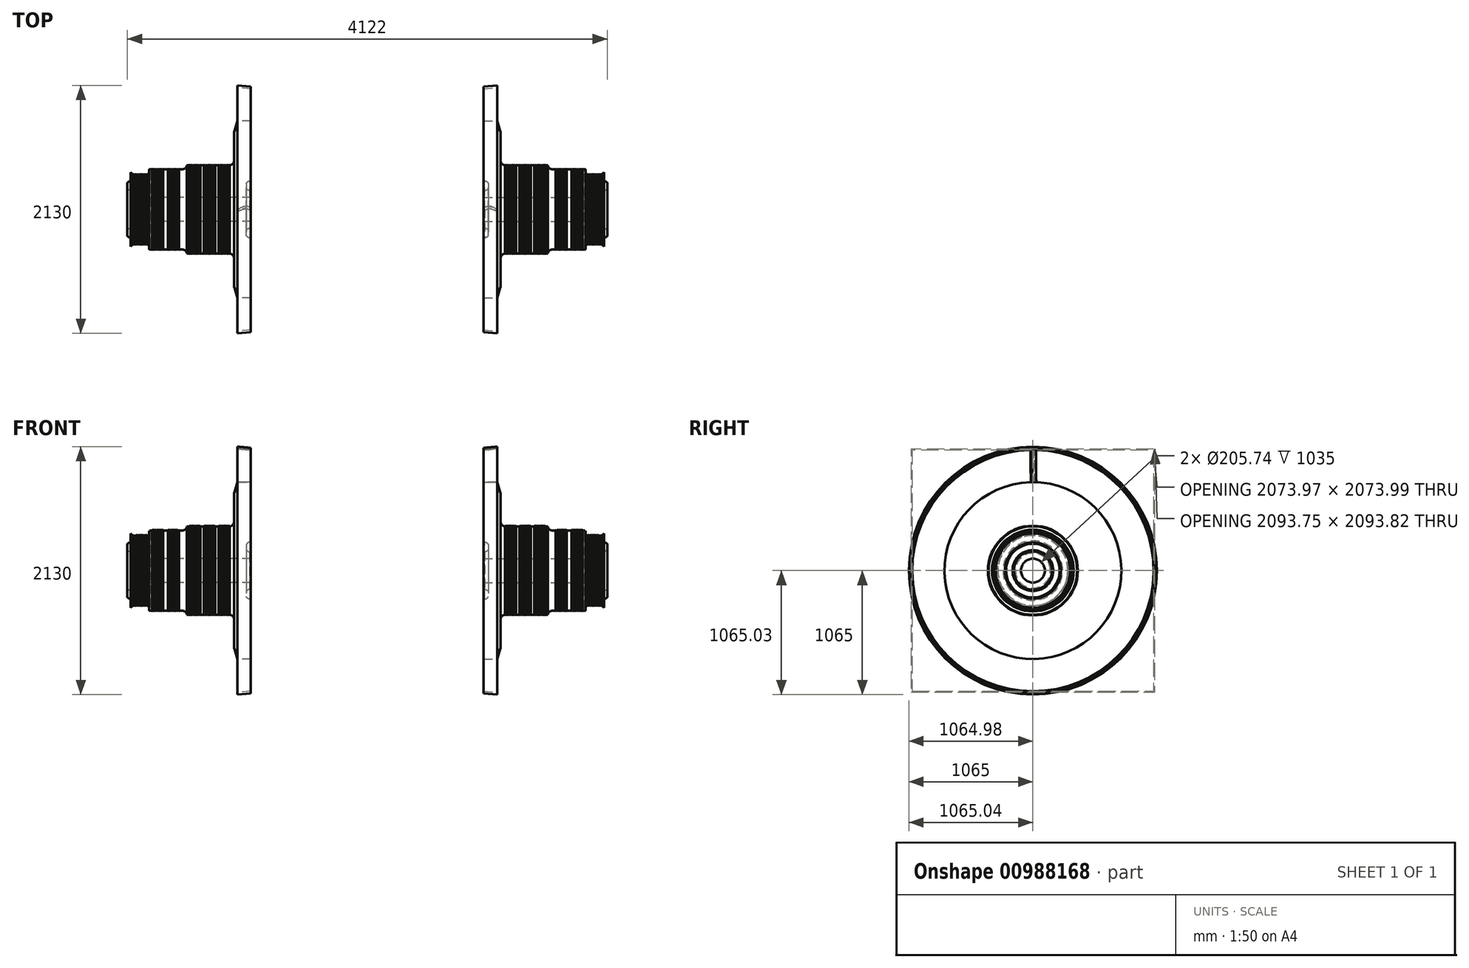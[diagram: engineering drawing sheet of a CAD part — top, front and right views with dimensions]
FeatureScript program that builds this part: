
annotation { "Feature Type Name" : "Feature", "Feature Type Description" : "" }
export const myFeature = defineFeature(function(context is Context, id is Id, definition is map)
    precondition{}
    {
        {
            var Q0;
            Q0=qCreatedBy(makeId("Top.planeOp"),FACE);
            var sketch = newSketch(context, id + "F0", { "sketchPlane" : qUnion([Q0])});
            skLineSegment(sketch, "E0", {"start": v(-458.73, 0) * mm, "end": v(0, 0) * mm, "construction": true});
            skLineSegment(sketch, "E1", {"start": v(0, 760) * mm, "end": v(-115, 760) * mm});
            skLineSegment(sketch, "E2", {"start": v(0, 102.87) * mm, "end": v(0, 157.87) * mm});
            skLineSegment(sketch, "E3", {"start": v(-115, 1065) * mm, "end": v(-115, 1047) * mm});
            skLineSegment(sketch, "E4", {"start": v(-115, 1047) * mm, "end": v(0, 1037) * mm});
            skLineSegment(sketch, "E5", {"start": v(0, 1037) * mm, "end": v(0, 1055) * mm});
            skLineSegment(sketch, "E6", {"start": v(0, 1055) * mm, "end": v(-115, 1065) * mm});
            skLineSegment(sketch, "E7", {"start": v(-115, 760) * mm, "end": v(-115, 1047) * mm, "construction": true});
            skLineSegment(sketch, "E8", {"start": v(-245, 202.87) * mm, "end": v(0, 202.87) * mm, "construction": true});
            skArc(sketch, "E9", {"start": v(0, 157.87) * mm, "mid": v(-22.53, 163.91) * mm, "end": v(-39, 180.42) * mm});
            skLineSegment(sketch, "E10", {"start": v(-39, 225.32) * mm, "end": v(-39, 180.42) * mm});
            skArc(sketch, "E11.trimOffspring", {"start": v(-39, 225.32) * mm, "mid": v(-22.53, 241.83) * mm, "end": v(0, 247.87) * mm});
            skLineSegment(sketch, "E12.trimOffspring", {"start": v(0, 247.87) * mm, "end": v(0, 760) * mm});
            skArc(sketch, "E13", {"start": v(0, 157.87) * mm, "mid": v(-45, 202.87) * mm, "end": v(0, 247.87) * mm, "construction": true});
            skLineSegment(sketch, "E14", {"start": v(0, 0) * mm, "end": v(1169.36, 0) * mm, "construction": true});
            skLineSegment(sketch, "E15", {"start": v(-115, 760) * mm, "end": v(-145, 665) * mm});
            skLineSegment(sketch, "E16", {"start": v(-145, 665) * mm, "end": v(-145, 380) * mm});
            skLineSegment(sketch, "E17", {"start": v(-145, 380) * mm, "end": v(-182, 380) * mm});
            skLineSegment(sketch, "E18", {"start": v(-550, 380) * mm, "end": v(-550, 345) * mm});
            skLineSegment(sketch, "E19", {"start": v(-550, 345) * mm, "end": v(-618, 345) * mm});
            skLineSegment(sketch, "E20", {"start": v(-870, 300) * mm, "end": v(-892, 300) * mm});
            skLineSegment(sketch, "E21", {"start": v(-1010, 300) * mm, "end": v(-1035, 320) * mm});
            skLineSegment(sketch, "E22", {"start": v(-1035, 320) * mm, "end": v(-1035, 240.87) * mm});
            skLineSegment(sketch, "E23", {"start": v(-1035, 102.87) * mm, "end": v(0, 102.87) * mm});
            skArc(sketch, "E24", {"start": v(-870, 345) * mm, "mid": v(-875, 340) * mm, "end": v(-870, 335) * mm});
            skLineSegment(sketch, "E25", {"start": v(-870, 335) * mm, "end": v(-870, 300) * mm});
            skLineSegment(sketch, "E26", {"start": v(-870, 345) * mm, "end": v(-870, 335) * mm, "construction": true});
            skLineSegment(sketch, "E27", {"start": v(-982, 306) * mm, "end": v(-898, 306) * mm, "construction": true});
            skLineSegment(sketch, "E28", {"start": v(-976, 300) * mm, "end": v(-970, 306) * mm});
            skLineSegment(sketch, "E29", {"start": v(-970, 306) * mm, "end": v(-964, 300) * mm});
            skLineSegment(sketch, "E30", {"start": v(-964, 300) * mm, "end": v(-958, 306) * mm});
            skLineSegment(sketch, "E31", {"start": v(-958, 306) * mm, "end": v(-952, 300) * mm});
            skLineSegment(sketch, "E32", {"start": v(-952, 300) * mm, "end": v(-946, 306) * mm});
            skLineSegment(sketch, "E33", {"start": v(-946, 306) * mm, "end": v(-940, 300) * mm});
            skLineSegment(sketch, "E34", {"start": v(-940, 300) * mm, "end": v(-934, 306) * mm});
            skLineSegment(sketch, "E35", {"start": v(-934, 306) * mm, "end": v(-928, 300) * mm});
            skLineSegment(sketch, "E36", {"start": v(-928, 300) * mm, "end": v(-922, 306) * mm});
            skLineSegment(sketch, "E37", {"start": v(-922, 306) * mm, "end": v(-916, 300) * mm});
            skLineSegment(sketch, "E38", {"start": v(-916, 300) * mm, "end": v(-910, 306) * mm});
            skLineSegment(sketch, "E39", {"start": v(-910, 306) * mm, "end": v(-904, 300) * mm});
            skPoint(sketch, "E40", {"position": v(-940, 300) * mm});
            skLineSegment(sketch, "E41", {"start": v(-976, 300) * mm, "end": v(-982, 306) * mm});
            skLineSegment(sketch, "E42", {"start": v(-982, 306) * mm, "end": v(-988, 300) * mm});
            skLineSegment(sketch, "E43", {"start": v(-904, 300) * mm, "end": v(-898, 306) * mm});
            skLineSegment(sketch, "E44", {"start": v(-898, 306) * mm, "end": v(-892, 300) * mm});
            skLineSegment(sketch, "E45.trimOffspring", {"start": v(-988, 300) * mm, "end": v(-1010, 300) * mm});
            skLineSegment(sketch, "E46", {"start": v(-844, 351) * mm, "end": v(-624, 351) * mm, "construction": true});
            skLineSegment(sketch, "E47", {"start": v(-850, 345) * mm, "end": v(-844, 351) * mm});
            skLineSegment(sketch, "E48", {"start": v(-844, 351) * mm, "end": v(-838, 345) * mm});
            skLineSegment(sketch, "E49", {"start": v(-838, 345) * mm, "end": v(-832, 351) * mm});
            skLineSegment(sketch, "E50", {"start": v(-832, 351) * mm, "end": v(-826, 345) * mm});
            skLineSegment(sketch, "E51", {"start": v(-826, 345) * mm, "end": v(-820, 351) * mm});
            skLineSegment(sketch, "E52", {"start": v(-820, 351) * mm, "end": v(-814, 345) * mm});
            skLineSegment(sketch, "E53", {"start": v(-814, 345) * mm, "end": v(-808, 351) * mm});
            skLineSegment(sketch, "E54", {"start": v(-808, 351) * mm, "end": v(-802, 345) * mm});
            skLineSegment(sketch, "E55", {"start": v(-802, 345) * mm, "end": v(-796, 351) * mm});
            skLineSegment(sketch, "E56", {"start": v(-796, 351) * mm, "end": v(-790, 345) * mm});
            skLineSegment(sketch, "E57", {"start": v(-790, 345) * mm, "end": v(-784, 351) * mm});
            skLineSegment(sketch, "E58", {"start": v(-784, 351) * mm, "end": v(-778, 345) * mm});
            skLineSegment(sketch, "E59", {"start": v(-778, 345) * mm, "end": v(-772, 351) * mm});
            skLineSegment(sketch, "E60", {"start": v(-772, 351) * mm, "end": v(-766, 345) * mm});
            skLineSegment(sketch, "E61", {"start": v(-766, 345) * mm, "end": v(-760, 351) * mm});
            skLineSegment(sketch, "E62", {"start": v(-760, 351) * mm, "end": v(-754, 345) * mm});
            skLineSegment(sketch, "E63.trimOffspring", {"start": v(-850, 345) * mm, "end": v(-870, 345) * mm});
            skLineSegment(sketch, "E64", {"start": v(-850, 345) * mm, "end": v(-754, 345) * mm, "construction": true});
            skLineSegment(sketch, "E65", {"start": v(-714, 345) * mm, "end": v(-708, 351) * mm});
            skLineSegment(sketch, "E66", {"start": v(-708, 351) * mm, "end": v(-702, 345) * mm});
            skLineSegment(sketch, "E67", {"start": v(-702, 345) * mm, "end": v(-696, 351) * mm});
            skLineSegment(sketch, "E68", {"start": v(-696, 351) * mm, "end": v(-690, 345) * mm});
            skLineSegment(sketch, "E69", {"start": v(-690, 345) * mm, "end": v(-684, 351) * mm});
            skLineSegment(sketch, "E70", {"start": v(-684, 351) * mm, "end": v(-678, 345) * mm});
            skLineSegment(sketch, "E71", {"start": v(-678, 345) * mm, "end": v(-672, 351) * mm});
            skLineSegment(sketch, "E72", {"start": v(-672, 351) * mm, "end": v(-666, 345) * mm});
            skLineSegment(sketch, "E73", {"start": v(-666, 345) * mm, "end": v(-660, 351) * mm});
            skLineSegment(sketch, "E74", {"start": v(-660, 351) * mm, "end": v(-654, 345) * mm});
            skLineSegment(sketch, "E75", {"start": v(-654, 345) * mm, "end": v(-648, 351) * mm});
            skLineSegment(sketch, "E76", {"start": v(-648, 351) * mm, "end": v(-642, 345) * mm});
            skLineSegment(sketch, "E77", {"start": v(-642, 345) * mm, "end": v(-636, 351) * mm});
            skLineSegment(sketch, "E78", {"start": v(-636, 351) * mm, "end": v(-630, 345) * mm});
            skLineSegment(sketch, "E79", {"start": v(-630, 345) * mm, "end": v(-624, 351) * mm});
            skLineSegment(sketch, "E80", {"start": v(-624, 351) * mm, "end": v(-618, 345) * mm});
            skLineSegment(sketch, "E81.trimOffspring", {"start": v(-714, 345) * mm, "end": v(-754, 345) * mm});
            skLineSegment(sketch, "E82", {"start": v(-524, 386) * mm, "end": v(415.47, 386) * mm, "construction": true});
            skLineSegment(sketch, "E83", {"start": v(-524, 386) * mm, "end": v(-530, 380) * mm});
            skLineSegment(sketch, "E84", {"start": v(-524, 386) * mm, "end": v(-518, 380) * mm});
            skLineSegment(sketch, "E85", {"start": v(-518, 380) * mm, "end": v(-512, 386) * mm});
            skLineSegment(sketch, "E86", {"start": v(-512, 386) * mm, "end": v(-506, 380) * mm});
            skLineSegment(sketch, "E87", {"start": v(-506, 380) * mm, "end": v(-500, 386) * mm});
            skLineSegment(sketch, "E88", {"start": v(-500, 386) * mm, "end": v(-494, 380) * mm});
            skLineSegment(sketch, "E89", {"start": v(-494, 380) * mm, "end": v(-488, 386) * mm});
            skLineSegment(sketch, "E90", {"start": v(-488, 386) * mm, "end": v(-482, 380) * mm});
            skLineSegment(sketch, "E91", {"start": v(-482, 380) * mm, "end": v(-476, 386) * mm});
            skLineSegment(sketch, "E92", {"start": v(-476, 386) * mm, "end": v(-470, 380) * mm});
            skLineSegment(sketch, "E93", {"start": v(-470, 380) * mm, "end": v(-464, 386) * mm});
            skLineSegment(sketch, "E94", {"start": v(-464, 386) * mm, "end": v(-458, 380) * mm});
            skLineSegment(sketch, "E95", {"start": v(-458, 380) * mm, "end": v(-452, 386) * mm});
            skLineSegment(sketch, "E96", {"start": v(-452, 386) * mm, "end": v(-446, 380) * mm});
            skLineSegment(sketch, "E97", {"start": v(-446, 380) * mm, "end": v(-440, 386) * mm});
            skLineSegment(sketch, "E98", {"start": v(-440, 386) * mm, "end": v(-434, 380) * mm});
            skLineSegment(sketch, "E99.trimOffspring", {"start": v(-530, 380) * mm, "end": v(-550, 380) * mm});
            skLineSegment(sketch, "E100", {"start": v(-404, 380) * mm, "end": v(-398, 386) * mm});
            skLineSegment(sketch, "E101", {"start": v(-398, 386) * mm, "end": v(-392, 380) * mm});
            skLineSegment(sketch, "E102", {"start": v(-392, 380) * mm, "end": v(-386, 386) * mm});
            skLineSegment(sketch, "E103", {"start": v(-386, 386) * mm, "end": v(-380, 380) * mm});
            skLineSegment(sketch, "E104", {"start": v(-380, 380) * mm, "end": v(-374, 386) * mm});
            skLineSegment(sketch, "E105", {"start": v(-374, 386) * mm, "end": v(-368, 380) * mm});
            skLineSegment(sketch, "E106", {"start": v(-368, 380) * mm, "end": v(-362, 386) * mm});
            skLineSegment(sketch, "E107", {"start": v(-362, 386) * mm, "end": v(-356, 380) * mm});
            skLineSegment(sketch, "E108", {"start": v(-356, 380) * mm, "end": v(-350, 386) * mm});
            skLineSegment(sketch, "E109", {"start": v(-350, 386) * mm, "end": v(-344, 380) * mm});
            skLineSegment(sketch, "E110", {"start": v(-344, 380) * mm, "end": v(-338, 386) * mm});
            skLineSegment(sketch, "E111", {"start": v(-338, 386) * mm, "end": v(-332, 380) * mm});
            skLineSegment(sketch, "E112", {"start": v(-332, 380) * mm, "end": v(-326, 386) * mm});
            skLineSegment(sketch, "E113", {"start": v(-326, 386) * mm, "end": v(-320, 380) * mm});
            skLineSegment(sketch, "E114", {"start": v(-320, 380) * mm, "end": v(-314, 386) * mm});
            skLineSegment(sketch, "E115", {"start": v(-314, 386) * mm, "end": v(-308, 380) * mm});
            skLineSegment(sketch, "E116.trimOffspring", {"start": v(-404, 380) * mm, "end": v(-434, 380) * mm});
            skLineSegment(sketch, "E117", {"start": v(-278, 380) * mm, "end": v(-272, 386) * mm});
            skLineSegment(sketch, "E118", {"start": v(-272, 386) * mm, "end": v(-266, 380) * mm});
            skLineSegment(sketch, "E119", {"start": v(-266, 380) * mm, "end": v(-260, 386) * mm});
            skLineSegment(sketch, "E120", {"start": v(-260, 386) * mm, "end": v(-254, 380) * mm});
            skLineSegment(sketch, "E121", {"start": v(-254, 380) * mm, "end": v(-248, 386) * mm});
            skLineSegment(sketch, "E122", {"start": v(-248, 386) * mm, "end": v(-242, 380) * mm});
            skLineSegment(sketch, "E123", {"start": v(-242, 380) * mm, "end": v(-236, 386) * mm});
            skLineSegment(sketch, "E124", {"start": v(-236, 386) * mm, "end": v(-230, 380) * mm});
            skLineSegment(sketch, "E125", {"start": v(-230, 380) * mm, "end": v(-224, 386) * mm});
            skLineSegment(sketch, "E126", {"start": v(-224, 386) * mm, "end": v(-218, 380) * mm});
            skLineSegment(sketch, "E127", {"start": v(-218, 380) * mm, "end": v(-212, 386) * mm});
            skLineSegment(sketch, "E128", {"start": v(-212, 386) * mm, "end": v(-206, 380) * mm});
            skLineSegment(sketch, "E129", {"start": v(-206, 380) * mm, "end": v(-200, 386) * mm});
            skLineSegment(sketch, "E130", {"start": v(-200, 386) * mm, "end": v(-194, 380) * mm});
            skLineSegment(sketch, "E131", {"start": v(-194, 380) * mm, "end": v(-188, 386) * mm});
            skLineSegment(sketch, "E132", {"start": v(-188, 386) * mm, "end": v(-182, 380) * mm});
            skLineSegment(sketch, "E133.trimOffspring", {"start": v(-278, 380) * mm, "end": v(-308, 380) * mm});
            skArc(sketch, "E134", {"start": v(-1035, 240.87) * mm, "mid": v(-1048.98, 238.2) * mm, "end": v(-1061, 230.58) * mm});
            skLineSegment(sketch, "E135.trimOffspring", {"start": v(-1035, 164.87) * mm, "end": v(-1035, 102.87) * mm});
            skLineSegment(sketch, "E136", {"start": v(-1061, 230.58) * mm, "end": v(-1061, 175.16) * mm});
            skArc(sketch, "E137.trimOffspring", {"start": v(-1061, 175.16) * mm, "mid": v(-1048.98, 167.54) * mm, "end": v(-1035, 164.87) * mm});
            skArc(sketch, "E138", {"start": v(-1035, 240.87) * mm, "mid": v(-1073, 202.87) * mm, "end": v(-1035, 164.87) * mm, "construction": true});
            skSolve(sketch);
        }
        {
            var Q0;
            Q0=makeQuery(id+"F0.imprint","IMPRINT",FACE,{"disambiguationData":[TD([[makeQuery(id+"F0.imprint","IMPRINT",EDGE,{"derivedFrom":sQuery(id+"F0.wireOp",EDGE,"E3")}),1.0]])]});
            var Q1;
            Q1=makeQuery(id+"F0.imprint","IMPRINT",FACE,{"disambiguationData":[TD([[makeQuery(id+"F0.imprint","IMPRINT",EDGE,{"derivedFrom":sQuery(id+"F0.wireOp",EDGE,"E1")}),1.0]])]});
            var Q2;
            Q2=sQuery(id+"F0.wireOp",EDGE,"E0");
            revolve(context, id + "F1", {"surfaceOperationType" : NewSurfaceOperationType.NEW, "entities" : qUnion([Q0, Q1]), "axis" : qUnion([Q2]), "revolveType" : RevolveType.FULL});
        }
        {
            var Q0;
            Q0=makeQuery(id+"F1.opRevolve","SWEPT_EDGE",EDGE,{"disambiguationData":[OSD([sQuery(id+"F0.wireOp",EDGE,"E11.trimOffspring"),sQuery(id+"F0.wireOp",EDGE,"E12.trimOffspring")])]});
            var Q1;
            Q1=makeQuery(id+"F1.opRevolve","SWEPT_EDGE",EDGE,{"disambiguationData":[OSD([sQuery(id+"F0.wireOp",EDGE,"E2"),sQuery(id+"F0.wireOp",EDGE,"E9")])]});
            chamfer(context, id + "F2", {"entities" : qUnion([Q0, Q1]), "width" : 9 * mm, "tangentPropagation" : true});
        }
        {
            var Q0;
            Q0=qCreatedBy(makeId("Right.planeOp"),FACE);
            var sketch = newSketch(context, id + "F3", { "sketchPlane" : qUnion([Q0])});
            skLineSegment(sketch, "E139", {"start": v(0, 0) * mm, "end": v(0, 760) * mm, "construction": true});
            skLineSegment(sketch, "E140", {"start": v(0, 0) * mm, "end": v(0, 1055) * mm, "construction": true});
            skCircle(sketch, "E141.0", {"center": v(0, 0) * mm, "radius": 1055 * mm, "construction": true});
            skCircle(sketch, "E142.0", {"center": v(0, 0) * mm, "radius": 760 * mm, "construction": true});
            skSolve(sketch);
        }
        {
            var Q0;
            Q0=sQuery(id+"F3.wireOp",VERTEX,"E140.end");
            var Q1;
            Q1=sQuery(id+"F3.wireOp",EDGE,"E140");
            cPlane(context, id + "F4", {"entities" : qUnion([Q0, Q1]), "cplaneType" : CPlaneType.LINE_POINT, "offset" : 25 * mm, "width" : 150 * mm, "height" : 150 * mm});
        }
        {
            var Q0;
            Q0=sQuery(id+"F3.wireOp",VERTEX,"E139.end");
            var Q1;
            Q1=sQuery(id+"F3.wireOp",EDGE,"E140");
            cPlane(context, id + "F5", {"entities" : qUnion([Q0, Q1]), "cplaneType" : CPlaneType.LINE_POINT, "offset" : 25 * mm, "width" : 150 * mm, "height" : 150 * mm});
        }
        {
            var Q0;
            Q0=qCreatedBy(id+"F5.planeOp",FACE);
            cPlane(context, id + "F6", {"entities" : qUnion([Q0]), "cplaneType" : CPlaneType.OFFSET, "offset" : 1 * mm, "oppositeDirection" : true, "width" : 150 * mm, "height" : 150 * mm});
        }
        {
            var Q0;
            Q0=qCreatedBy(id+"F4.planeOp",FACE);
            cPlane(context, id + "F7", {"entities" : qUnion([Q0]), "cplaneType" : CPlaneType.OFFSET, "offset" : 5 * mm, "oppositeDirection" : true, "width" : 150 * mm, "height" : 150 * mm});
        }
        {
            var Q0;
            Q0=qCreatedBy(id+"F6.planeOp",FACE);
            var sketch = newSketch(context, id + "F8", { "sketchPlane" : qUnion([Q0])});
            skLineSegment(sketch, "E143.0", {"start": v(0, 760) * mm, "end": v(0, -760) * mm, "construction": true});
            skLineSegment(sketch, "E144", {"start": v(0, 0) * mm, "end": v(0, 15) * mm});
            skLineSegment(sketch, "E145", {"start": v(-115, -7.83) * mm, "end": v(-115, -17.83) * mm});
            skFitSpline(sketch, "E146", {"points": [v(0, 15) * mm, v(-23.34, 27.04) * mm, v(-65.87, 24.4) * mm, v(-115, -7.83) * mm], "startDerivative": vector(-98.33, 77.82) * mm, "endDerivative": vector(-58.12, -78.29) * mm});
            skFitSpline(sketch, "E147", {"points": [v(0, 0) * mm, v(-12.16, -4.34) * mm, v(-46.89, 7.32) * mm, v(-115, -17.83) * mm], "startDerivative": vector(-36.35, -51.97) * mm, "endDerivative": vector(-97, -78.68) * mm});
            skLineSegment(sketch, "E148.0", {"start": v(-115, -760) * mm, "end": v(-115, 760) * mm, "construction": true});
            skSolve(sketch);
        }
        {
            var Q0;
            Q0=qCreatedBy(id+"F7.planeOp",FACE);
            var sketch = newSketch(context, id + "F9", { "sketchPlane" : qUnion([Q0])});
            skLineSegment(sketch, "E149.0", {"start": v(0, 1055) * mm, "end": v(0, -1055) * mm, "construction": true});
            skLineSegment(sketch, "E150.0", {"start": v(-115, -1065) * mm, "end": v(-115, 1065) * mm, "construction": true});
            skLineSegment(sketch, "E151", {"start": v(-115, -10.92) * mm, "end": v(-115, -20.92) * mm});
            skLineSegment(sketch, "E152", {"start": v(0, 12.03) * mm, "end": v(0, -2.97) * mm});
            skFitSpline(sketch, "E153", {"points": [v(0, 12.03) * mm, v(-23.93, 24.4) * mm, v(-65.13, 22.33) * mm, v(-115, -10.92) * mm], "startDerivative": vector(-60.38, 73.82) * mm, "endDerivative": vector(-114.64, -123.6) * mm});
            skFitSpline(sketch, "E154", {"points": [v(0, -2.97) * mm, v(-16.28, -8.13) * mm, v(-46.89, 3.8) * mm, v(-115, -20.92) * mm], "startDerivative": vector(-80.99, -68.84) * mm, "endDerivative": vector(-115.2, -76.2) * mm});
            skSolve(sketch);
        }
        {
            var Q2;
            Q2=qSketchRegion(id+"F8",true);
            var Q3;
            Q3=qSketchRegion(id+"F9",true);
            loft(context, id + "F10", {"operationType" : NewBodyOperationType.ADD, "sheetProfilesArray" : [{ "sheetProfileEntities" : qUnion([Q2]) }, { "sheetProfileEntities" : qUnion([Q3]) }]});
        }
        {
            var Q0;
            Q0=makeQuery(id+"F1.opRevolve","SWEPT_EDGE",EDGE,{"disambiguationData":[OSD([sQuery(id+"F0.wireOp",EDGE,"E16"),sQuery(id+"F0.wireOp",EDGE,"E17")])]});
            var Q1;
            Q1=makeQuery(id+"F1.opRevolve","SWEPT_EDGE",EDGE,{"disambiguationData":[OSD([sQuery(id+"F0.wireOp",EDGE,"E18"),sQuery(id+"F0.wireOp",EDGE,"E19")])]});
            fillet(context, id + "F11", {"entities" : qUnion([Q0, Q1]), "tangentPropagation" : true, "radius" : 40 * mm, "defaultsChanged" : true, "vertexSettings" : [], "allowEdgeOverflow" : false});
        }
        {
            var Q0;
            Q0=makeQuery(id+"F1.opRevolve","SWEPT_EDGE",EDGE,{"disambiguationData":[OSD([sQuery(id+"F0.wireOp",EDGE,"E20"),sQuery(id+"F0.wireOp",EDGE,"E25")])]});
            fillet(context, id + "F12", {"entities" : qUnion([Q0]), "tangentPropagation" : true, "radius" : 30 * mm, "defaultsChanged" : true, "vertexSettings" : [], "allowEdgeOverflow" : false});
        }
        {
            var Q0;
            Q0=makeQuery(id+"F1.opRevolve","SWEPT_EDGE",EDGE,{"disambiguationData":[OSD([sQuery(id+"F0.wireOp",EDGE,"E15"),sQuery(id+"F0.wireOp",EDGE,"E16")])]});
            fillet(context, id + "F13", {"entities" : qUnion([Q0]), "tangentPropagation" : true, "radius" : 50 * mm, "defaultsChanged" : true, "vertexSettings" : [], "allowEdgeOverflow" : false});
        }
        {
            var Q0;
            Q0=qCreatedBy(makeId("Right.planeOp"),FACE);
            cPlane(context, id + "F14", {"entities" : qUnion([Q0]), "cplaneType" : CPlaneType.OFFSET, "offset" : 1000 * mm, "width" : 150 * mm, "height" : 150 * mm});
        }
        {
            var Q0;
            Q0=makeQuery(id+"F1.opRevolve","SWEPT_BODY",BODY,{"disambiguationData":[OSD([sQuery(id+"F0.wireOp",EDGE,"E1"),sQuery(id+"F0.wireOp",EDGE,"8eOnuTwe-mc4H-67do-FhrC-v4fiDaNp4USt"),sQuery(id+"F0.wireOp",EDGE,"85Pv9K4k-QK6J-0Qlt-xgkq-tkcUd5Xrmcca"),sQuery(id+"F0.wireOp",EDGE,"nWjtiG4I-wXqO-Cc5y-gf5R-kpWSPuTRreDN"),sQuery(id+"F0.wireOp",EDGE,"8BdgWwB3-doG2-UeEC-EHoW-rA4jYJ7YKrnq"),sQuery(id+"F0.wireOp",EDGE,"E2"),sQuery(id+"F0.wireOp",EDGE,"pvBcjrHt-OPn6-X4Kq-pzX3-374l1QbR4QxP"),sQuery(id+"F0.wireOp",EDGE,"49UQ9rEw-xUfE-Qjs9-t7rO-eBe6l5RDYJrW"),sQuery(id+"F0.wireOp",EDGE,"fxrR5Uu6-hcaA-7ZeZ-MwSR-YCVFVn7EG2iE"),sQuery(id+"F0.wireOp",EDGE,"Frn25Btm-aShf-nTfp-R7bq-ZnN7MAH42RaJ"),sQuery(id+"F0.wireOp",EDGE,"WgH4X2lM-l7hA-AiIu-9NEw-SN8PY96Z6mnh"),sQuery(id+"F0.wireOp",EDGE,"f5b9e493-137a-46cc-8c53-4f8538a639c1.trimOffspring"),sQuery(id+"F0.wireOp",EDGE,"8439ef33-02f7-44c0-801c-3169d5dbefe9.trimOffspring"),sQuery(id+"F0.wireOp",EDGE,"E9"),sQuery(id+"F0.wireOp",EDGE,"E10"),sQuery(id+"F0.wireOp",EDGE,"E11.trimOffspring"),sQuery(id+"F0.wireOp",EDGE,"E12.trimOffspring")])]});
            var Q1;
            Q1=qCreatedBy(id+"F14.planeOp",FACE);
            mirror(context, id + "F15", {"entities" : qUnion([Q0]), "mirrorPlane" : qUnion([Q1])});
        }
    });
